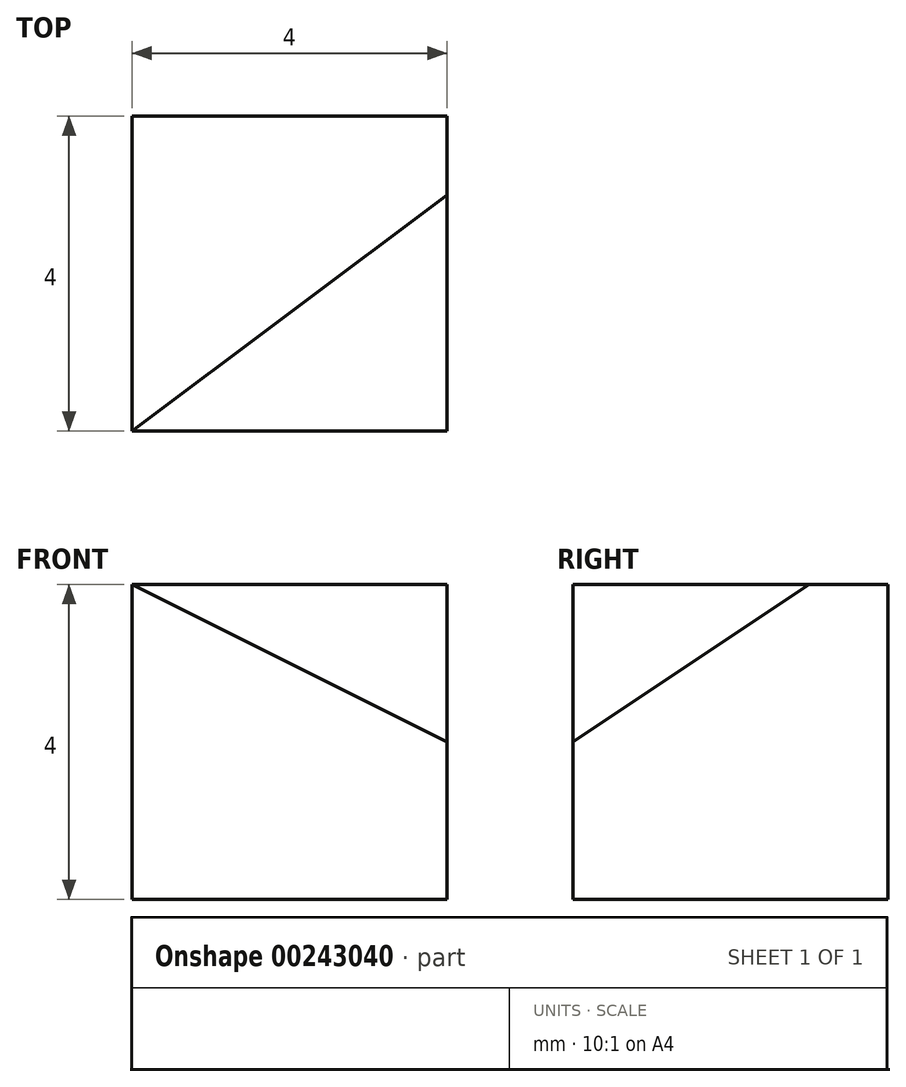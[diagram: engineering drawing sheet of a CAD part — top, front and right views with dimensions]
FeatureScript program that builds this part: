
annotation { "Feature Type Name" : "Feature", "Feature Type Description" : "" }
export const myFeature = defineFeature(function(context is Context, id is Id, definition is map)
    precondition{}
    {
        {
            var Q0;
            Q0=qCreatedBy(makeId("Top.planeOp"),FACE);
            var sketch = newSketch(context, id + "F0", { "sketchPlane" : qUnion([Q0])});
            skLineSegment(sketch, "E0.bottom", {"start": v(0, 0) * mm, "end": v(4, 0) * mm});
            skLineSegment(sketch, "E0.top", {"start": v(0, 4) * mm, "end": v(4, 4) * mm});
            skLineSegment(sketch, "E0.left", {"start": v(0, 0) * mm, "end": v(0, 4) * mm});
            skLineSegment(sketch, "E0.right", {"start": v(4, 0) * mm, "end": v(4, 4) * mm});
            skSolve(sketch);
        }
        {
            var Q0;
            Q0 = qSketchRegion(id + "F0", true);
            extrude(context, id + "F1", {"entities" : qUnion([Q0]), "depth" : 4 * mm});
        }
        {
            var Q0;
            Q0=makeQuery(id+"F1.opExtrude","SWEPT_FACE",FACE,{"disambiguationData":[OSD([sQuery(id+"F0.wireOp",EDGE,"E0.right")])]});
            var sketch = newSketch(context, id + "F2", { "sketchPlane" : qUnion([Q0])});
            skLineSegment(sketch, "E1", {"start": v(4, 4) * mm, "end": v(3, 4) * mm, "construction": true});
            skLineSegment(sketch, "E2", {"start": v(3, 4) * mm, "end": v(0, 2) * mm, "construction": true});
            skSolve(sketch);
        }
        {
            var Q0;
            Q0=sQuery(id+"F2.wireOp",VERTEX,"E2.start");
            var Q1;
            Q1=makeQuery(id+"F1.opExtrude","CAP_VERTEX",VERTEX,{"disambiguationData":[OSD([sQuery(id+"F0.wireOp",EDGE,"E0.bottom"),sQuery(id+"F0.wireOp",EDGE,"E0.left")])],"isStart":false});
            var Q2;
            Q2=sQuery(id+"F2.wireOp",VERTEX,"E2.end");
            cPlane(context, id + "F3", {"entities" : qUnion([Q0, Q1, Q2]), "cplaneType" : CPlaneType.THREE_POINT, "offset" : 25 * mm, "width" : 150 * mm, "height" : 150 * mm});
        }
        {
            var Q0;
            Q0=qCreatedBy(id+"F3.planeOp",FACE);
            var sketch = newSketch(context, id + "F4", { "sketchPlane" : qUnion([Q0])});
            skPoint(sketch, "E3.0", {"position": v(3.05, -1.1) * mm});
            skPoint(sketch, "E4.0", {"position": v(3.05, -4.71) * mm});
            skPoint(sketch, "E5.0", {"position": v(-1.28, -2.22) * mm});
            skLineSegment(sketch, "E6", {"start": v(-1.28, -2.22) * mm, "end": v(3.05, -1.1) * mm});
            skLineSegment(sketch, "E7", {"start": v(3.05, -4.71) * mm, "end": v(-1.28, -2.22) * mm});
            skLineSegment(sketch, "E8", {"start": v(3.05, -1.1) * mm, "end": v(3.05, -4.71) * mm});
            skSolve(sketch);
        }
        {
            var Q0;
            Q0 = qSketchRegion(id + "F4", true);
            extrude(context, id + "F5", {"entities" : qUnion([Q0]), "operationType" : NewBodyOperationType.REMOVE, "oppositeDirection" : true, "depth" : 25 * mm});
        }
    });
